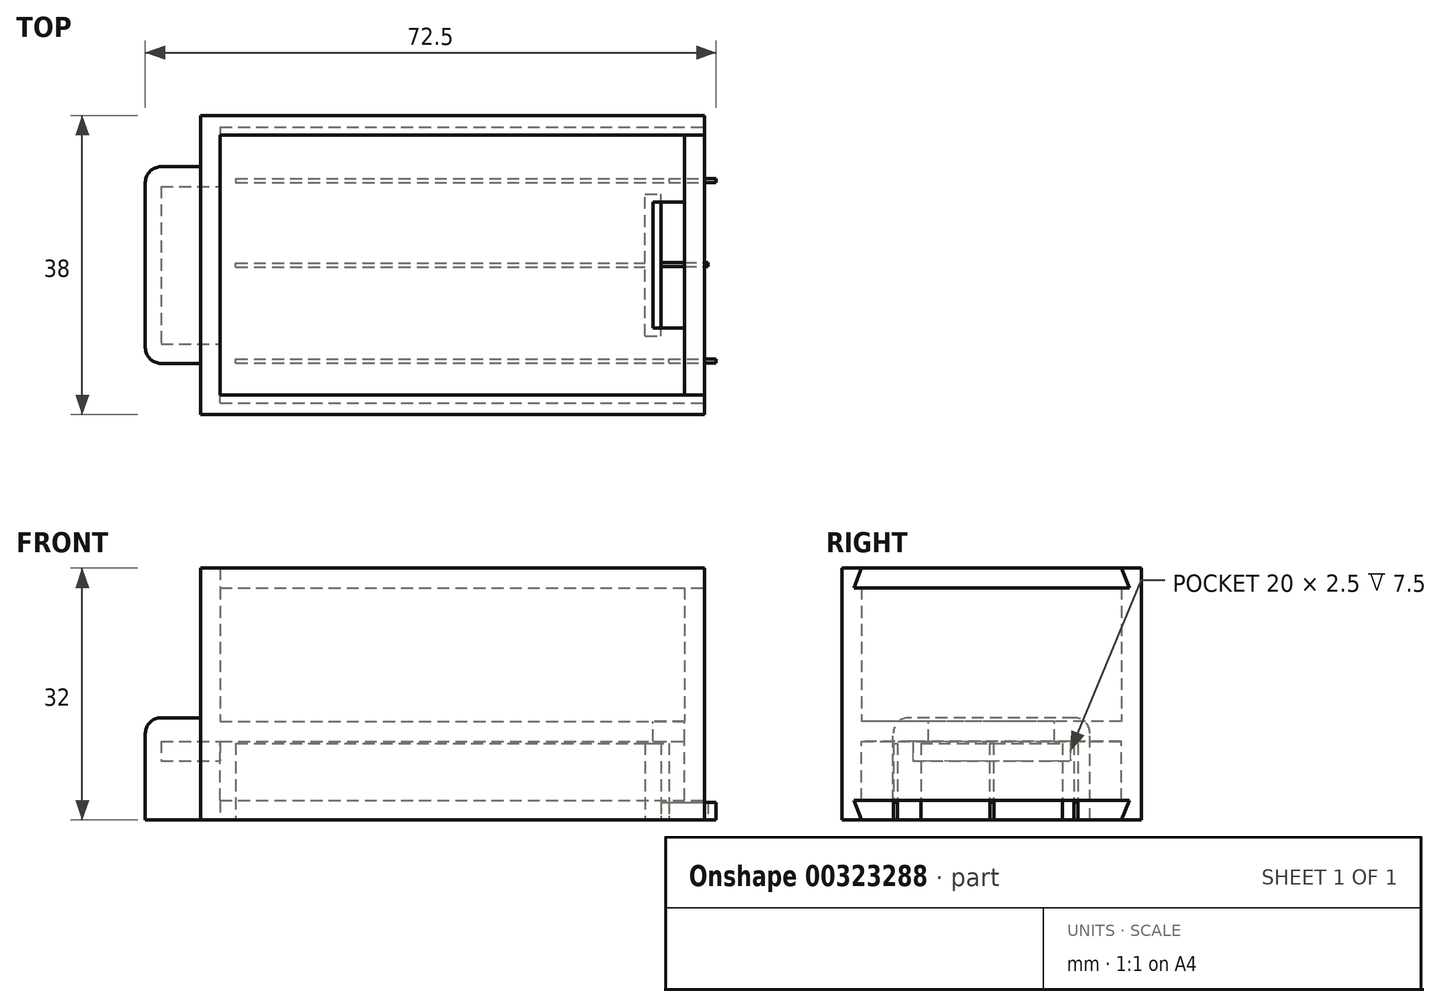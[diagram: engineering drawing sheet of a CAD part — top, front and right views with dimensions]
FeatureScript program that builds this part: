
annotation { "Feature Type Name" : "Feature", "Feature Type Description" : "" }
export const myFeature = defineFeature(function(context is Context, id is Id, definition is map)
    precondition{}
    {
        {
            var Q0;
            Q0=qCreatedBy(makeId("Top.planeOp"),FACE);
            var sketch = newSketch(context, id + "F0", { "sketchPlane" : qUnion([Q0])});
            skLineSegment(sketch, "E0.bottom", {"start": v(-32, 19) * mm, "end": v(32, 19) * mm});
            skLineSegment(sketch, "E0.top", {"start": v(-32, -19) * mm, "end": v(32, -19) * mm});
            skLineSegment(sketch, "E0.left", {"start": v(-32, 19) * mm, "end": v(-32, -19) * mm});
            skLineSegment(sketch, "E0.right", {"start": v(32, 19) * mm, "end": v(32, -19) * mm});
            skPoint(sketch, "E1", {"position": v(32, 0) * mm});
            skPoint(sketch, "E2", {"position": v(0, -19) * mm});
            skSolve(sketch);
        }
        {
            var Q0;
            Q0=makeQuery(id+"F0.imprint","IMPRINT",FACE,{"disambiguationData":[TD([[makeQuery(id+"F0.imprint","IMPRINT",EDGE,{"derivedFrom":sQuery(id+"F0.wireOp",EDGE,"E0.bottom")}),-1.0]])]});
            extrude(context, id + "F1", {"entities" : qUnion([Q0]), "depth" : 22 * mm});
        }
        {
            var Q0;
            Q0=makeQuery(id+"F1.opExtrude","CAP_FACE",FACE,{"disambiguationData":[OSD([sQuery(id+"F0.wireOp",EDGE,"E0.bottom"),sQuery(id+"F0.wireOp",EDGE,"E0.top"),sQuery(id+"F0.wireOp",EDGE,"E0.left"),sQuery(id+"F0.wireOp",EDGE,"E0.right")])],"isStart":false});
            shell(context, id + "F2", {"entities" : qUnion([Q0]), "thickness" : 2.5 * mm});
        }
        {
            var Q0;
            Q0=makeQuery(id+"F1.opExtrude","SWEPT_FACE",FACE,{"disambiguationData":[OSD([sQuery(id+"F0.wireOp",EDGE,"E0.right")])]});
            var sketch = newSketch(context, id + "F3", { "sketchPlane" : qUnion([Q0])});
            skLineSegment(sketch, "E3.bottom", {"start": v(19, 22) * mm, "end": v(-19, 22) * mm});
            skLineSegment(sketch, "E3.top", {"start": v(19, 19.5) * mm, "end": v(-19, 19.5) * mm});
            skLineSegment(sketch, "E3.left", {"start": v(19, 22) * mm, "end": v(19, 19.5) * mm});
            skLineSegment(sketch, "E3.right", {"start": v(-19, 22) * mm, "end": v(-19, 19.5) * mm});
            skPoint(sketch, "E4", {"position": v(17.5, 19.5) * mm});
            skPoint(sketch, "E5", {"position": v(-17.5, 19.5) * mm});
            skLineSegment(sketch, "E6", {"start": v(-16.5, 22) * mm, "end": v(-17.5, 19.5) * mm});
            skLineSegment(sketch, "E7", {"start": v(16.5, 22) * mm, "end": v(17.5, 19.5) * mm});
            skLineSegment(sketch, "E8", {"start": v(-17.2, 19.5) * mm, "end": v(-16.2, 22) * mm});
            skLineSegment(sketch, "E9", {"start": v(17.2, 19.5) * mm, "end": v(16.2, 22) * mm});
            skSolve(sketch);
        }
        {
            var Q0;
            {var subQ0=sQuery(id+"F3.wireOp",EDGE,"E7");Q0=makeQuery(id+"F3.imprint","IMPRINT",FACE,{"disambiguationData":[TD([[makeQuery(id+"F3.imprint","IMPRINT",EDGE,{"derivedFrom":subQ0}),-1.0]])]});}
            var Q1;
            {var subQ0=sQuery(id+"F3.wireOp",EDGE,"E8");Q1=makeQuery(id+"F3.imprint","IMPRINT",FACE,{"disambiguationData":[TD([[makeQuery(id+"F3.imprint","IMPRINT",EDGE,{"derivedFrom":subQ0}),-1.0]])]});}
            var Q2;
            {var subQ0=sQuery(id+"F3.wireOp",EDGE,"E6");Q2=makeQuery(id+"F3.imprint","IMPRINT",FACE,{"disambiguationData":[TD([[makeQuery(id+"F3.imprint","IMPRINT",EDGE,{"derivedFrom":subQ0}),1.0]])]});}
            var Q3;
            {var subQ0=sQuery(id+"F0.wireOp",EDGE,"E0.left");var subQ1=sQuery(id+"F0.wireOp",EDGE,"E0.bottom");Q3=makeQuery(id+"F2.opShell","OFFSET_VERTEX",VERTEX,{"disambiguationData":[OSD([subQ1,subQ0]),TDD([makeQuery(id+"F1.opExtrude","CAP_VERTEX",VERTEX,{"disambiguationData":[OSD([subQ1,subQ0])],"isStart":false})])]});}
            extrude(context, id + "F4", {"entities" : qUnion([Q0, Q1, Q2]), "operationType" : NewBodyOperationType.REMOVE, "endBound" : BoundingType.UP_TO_VERTEX, "oppositeDirection" : true, "endBoundEntityVertex" : qUnion([Q3]), "depth" : 25 * mm});
        }
        {
            var Q0;
            {var subQ0=sQuery(id+"F3.wireOp",EDGE,"E8");Q0=makeQuery(id+"F3.imprint","IMPRINT",FACE,{"disambiguationData":[TD([[makeQuery(id+"F3.imprint","IMPRINT",EDGE,{"derivedFrom":subQ0}),-1.0]])]});}
            var Q1;
            {var subQ0=sQuery(id+"F0.wireOp",EDGE,"E0.left");var subQ1=sQuery(id+"F0.wireOp",EDGE,"E0.bottom");Q1=makeQuery(id+"F4.boolean.opBoolean","MERGE",VERTEX,{"derivedFrom":[makeQuery(id+"F2.opShell","OFFSET_VERTEX",VERTEX,{"disambiguationData":[OSD([subQ1,subQ0]),TDD([makeQuery(id+"F1.opExtrude","CAP_VERTEX",VERTEX,{"disambiguationData":[OSD([subQ1,subQ0])],"isStart":false})])]})],"fromTools":[makeQuery(id+"F4.opExtrude","CAP_VERTEX",VERTEX,{"disambiguationData":[OSD([sQuery(id+"F3.wireOp",EDGE,"E3.bottom"),sQuery(id+"F3.wireOp",EDGE,"E7")])],"isStart":false})]});}
            extrude(context, id + "F5", {"entities" : qUnion([Q0]), "endBound" : BoundingType.UP_TO_VERTEX, "oppositeDirection" : true, "endBoundEntityVertex" : qUnion([Q1]), "depth" : 25 * mm});
        }
        {
            var Q0;
            Q0=makeQuery(id+"F2.opShell","OFFSET_FACE",FACE,{"disambiguationData":[OSD([sQuery(id+"F0.wireOp",EDGE,"E0.bottom"),sQuery(id+"F0.wireOp",EDGE,"E0.top"),sQuery(id+"F0.wireOp",EDGE,"E0.left"),sQuery(id+"F0.wireOp",EDGE,"E0.right")])]});
            var sketch = newSketch(context, id + "F6", { "sketchPlane" : qUnion([Q0])});
            skLineSegment(sketch, "E10.bottom", {"start": v(29.5, 8) * mm, "end": v(25.5, 8) * mm});
            skLineSegment(sketch, "E10.top", {"start": v(29.5, -8) * mm, "end": v(25.5, -8) * mm});
            skLineSegment(sketch, "E10.left", {"start": v(29.5, 8) * mm, "end": v(29.5, -8) * mm});
            skLineSegment(sketch, "E10.right", {"start": v(25.5, 8) * mm, "end": v(25.5, -8) * mm});
            skPoint(sketch, "E11", {"position": v(29.5, 0) * mm});
            skSolve(sketch);
        }
        {
            var Q0;
            Q0=makeQuery(id+"F6.imprint","IMPRINT",FACE,{"disambiguationData":[TD([[makeQuery(id+"F6.imprint","IMPRINT",EDGE,{"derivedFrom":sQuery(id+"F6.wireOp",EDGE,"E10.bottom")}),1.0]])]});
            var Q1;
            Q1=makeQuery(id+"F1.opExtrude","CAP_FACE",FACE,{"disambiguationData":[OSD([sQuery(id+"F0.wireOp",EDGE,"E0.bottom"),sQuery(id+"F0.wireOp",EDGE,"E0.top"),sQuery(id+"F0.wireOp",EDGE,"E0.left"),sQuery(id+"F0.wireOp",EDGE,"E0.right")])],"isStart":true});
            extrude(context, id + "F7", {"entities" : qUnion([Q0]), "operationType" : NewBodyOperationType.REMOVE, "endBound" : BoundingType.UP_TO_SURFACE, "oppositeDirection" : true, "endBoundEntityFace" : qUnion([Q1]), "depth" : 25 * mm});
        }
        {
            var Q0;
            Q0=makeQuery(id+"F1.opExtrude","CAP_FACE",FACE,{"disambiguationData":[OSD([sQuery(id+"F0.wireOp",EDGE,"E0.bottom"),sQuery(id+"F0.wireOp",EDGE,"E0.top"),sQuery(id+"F0.wireOp",EDGE,"E0.left"),sQuery(id+"F0.wireOp",EDGE,"E0.right")])],"isStart":true});
            var sketch = newSketch(context, id + "F8", { "sketchPlane" : qUnion([Q0])});
            skLineSegment(sketch, "E12.0", {"start": v(-29.5, 16.5) * mm, "end": v(29.5, 16.5) * mm});
            skLineSegment(sketch, "E12.1", {"start": v(-29.5, -16.5) * mm, "end": v(-29.5, 16.5) * mm});
            skLineSegment(sketch, "E12.2", {"start": v(-29.5, -16.5) * mm, "end": v(29.5, -16.5) * mm});
            skLineSegment(sketch, "E12.3", {"start": v(29.5, -16.5) * mm, "end": v(29.5, 16.5) * mm});
            skSolve(sketch);
        }
        {
            var Q0;
            {var subQ8=sQuery(id+"F8.wireOp",EDGE,"E12.0");Q0=makeQuery(id+"F8.imprint","IMPRINT",FACE,{"disambiguationData":[TD([[makeQuery(id+"F8.imprint","IMPRINT",EDGE,{"derivedFrom":subQ8}),1.0]])]});}
            extrude(context, id + "F9", {"entities" : qUnion([Q0]), "operationType" : NewBodyOperationType.ADD, "depth" : 10 * mm});
        }
        {
            var Q0;
            Q0=makeQuery(id+"F9.opExtrude","SWEPT_FACE",FACE,{"disambiguationData":[OSD([sQuery(id+"F8.wireOp",EDGE,"E12.1")])]});
            var sketch = newSketch(context, id + "F10", { "sketchPlane" : qUnion([Q0])});
            skLineSegment(sketch, "E13.bottom", {"start": v(-10, 0) * mm, "end": v(10, 0) * mm});
            skLineSegment(sketch, "E13.top", {"start": v(-10, -2.5) * mm, "end": v(10, -2.5) * mm});
            skLineSegment(sketch, "E13.left", {"start": v(-10, 0) * mm, "end": v(-10, -2.5) * mm});
            skLineSegment(sketch, "E13.right", {"start": v(10, 0) * mm, "end": v(10, -2.5) * mm});
            skPoint(sketch, "E14", {"position": v(0, 0) * mm});
            skSolve(sketch);
        }
        {
            var Q0;
            Q0=makeQuery(id+"F10.imprint","IMPRINT",FACE,{"disambiguationData":[TD([[makeQuery(id+"F10.imprint","IMPRINT",EDGE,{"derivedFrom":sQuery(id+"F10.wireOp",EDGE,"E13.bottom")}),1.0]])]});
            extrude(context, id + "F11", {"entities" : qUnion([Q0]), "operationType" : NewBodyOperationType.REMOVE, "endBound" : BoundingType.THROUGH_ALL, "oppositeDirection" : true, "depth" : 25 * mm});
        }
        {
            var Q0;
            {var subQ0=sQuery(id+"F0.wireOp",EDGE,"E0.right");Q0=makeQuery(id+"F9.boolean.opBoolean","MERGE",FACE,{"derivedFrom":[makeQuery(id+"F1.opExtrude","SWEPT_FACE",FACE,{"disambiguationData":[OSD([subQ0])]}),makeQuery(id+"F9.opExtrude","SWEPT_FACE",FACE,{"disambiguationData":[OSD([subQ0])]})]});}
            var sketch = newSketch(context, id + "F12", { "sketchPlane" : qUnion([Q0])});
            skLineSegment(sketch, "E15", {"start": v(-19, -7.5) * mm, "end": v(19, -7.5) * mm});
            skLineSegment(sketch, "E16", {"start": v(-17.5, -7.5) * mm, "end": v(-16.5, -10) * mm});
            skLineSegment(sketch, "E17", {"start": v(17.5, -7.5) * mm, "end": v(16.5, -10) * mm});
            skLineSegment(sketch, "E18", {"start": v(-17.2, -7.5) * mm, "end": v(-16.2, -10) * mm});
            skLineSegment(sketch, "E19", {"start": v(17.2, -7.5) * mm, "end": v(16.2, -10) * mm});
            skSolve(sketch);
        }
        {
            var Q0;
            {var subQ0=sQuery(id+"F12.wireOp",EDGE,"E18");Q0=makeQuery(id+"F12.imprint","IMPRINT",FACE,{"disambiguationData":[TD([[makeQuery(id+"F12.imprint","IMPRINT",EDGE,{"derivedFrom":subQ0}),1.0]])]});}
            var Q1;
            {var subQ0=sQuery(id+"F12.wireOp",EDGE,"E17");Q1=makeQuery(id+"F12.imprint","IMPRINT",FACE,{"disambiguationData":[TD([[makeQuery(id+"F12.imprint","IMPRINT",EDGE,{"derivedFrom":subQ0}),-1.0]])]});}
            var Q2;
            {var subQ0=sQuery(id+"F12.wireOp",EDGE,"E16");Q2=makeQuery(id+"F12.imprint","IMPRINT",FACE,{"disambiguationData":[TD([[makeQuery(id+"F12.imprint","IMPRINT",EDGE,{"derivedFrom":subQ0}),1.0]])]});}
            var Q3;
            Q3=makeQuery(id+"F9.opExtrude","SWEPT_FACE",FACE,{"disambiguationData":[OSD([sQuery(id+"F8.wireOp",EDGE,"E12.1")])]});
            extrude(context, id + "F13", {"entities" : qUnion([Q0, Q1, Q2]), "operationType" : NewBodyOperationType.REMOVE, "endBound" : BoundingType.UP_TO_SURFACE, "oppositeDirection" : true, "endBoundEntityFace" : qUnion([Q3]), "depth" : 25 * mm});
        }
        {
            var Q0;
            {var subQ0=sQuery(id+"F12.wireOp",EDGE,"E18");Q0=makeQuery(id+"F12.imprint","IMPRINT",FACE,{"disambiguationData":[TD([[makeQuery(id+"F12.imprint","IMPRINT",EDGE,{"derivedFrom":subQ0}),1.0]])]});}
            var Q1;
            Q1=makeQuery(id+"F13.boolean.opBoolean","MERGE",FACE,{"derivedFrom":[makeQuery(id+"F9.opExtrude","SWEPT_FACE",FACE,{"disambiguationData":[OSD([sQuery(id+"F8.wireOp",EDGE,"E12.1")])]})],"fromTools":[makeQuery(id+"F13.opExtrude","CAP_FACE",FACE,{"disambiguationData":[OSD([sQuery(id+"F0.wireOp",EDGE,"E0.right"),sQuery(id+"F12.wireOp",EDGE,"E15"),sQuery(id+"F12.wireOp",EDGE,"E16"),sQuery(id+"F12.wireOp",EDGE,"E17")])],"isStart":false})]});
            extrude(context, id + "F14", {"entities" : qUnion([Q0]), "endBound" : BoundingType.UP_TO_SURFACE, "oppositeDirection" : true, "endBoundEntityFace" : qUnion([Q1]), "depth" : 25 * mm});
        }
        {
            var Q0;
            Q0=makeQuery(id+"F9.opExtrude","CAP_FACE",FACE,{"disambiguationData":[OSD([sQuery(id+"F0.wireOp",EDGE,"E0.bottom"),sQuery(id+"F0.wireOp",EDGE,"E0.top"),sQuery(id+"F0.wireOp",EDGE,"E0.left"),sQuery(id+"F0.wireOp",EDGE,"E0.right"),sQuery(id+"F8.wireOp",EDGE,"E12.0"),sQuery(id+"F8.wireOp",EDGE,"E12.1"),sQuery(id+"F8.wireOp",EDGE,"E12.2"),sQuery(id+"F8.wireOp",EDGE,"E12.3")])],"isStart":false});
            var sketch = newSketch(context, id + "F15", { "sketchPlane" : qUnion([Q0])});
            skPoint(sketch, "E20.0", {"position": v(25.5, -8) * mm});
            skPoint(sketch, "E20.1", {"position": v(25.5, 8) * mm});
            skLineSegment(sketch, "E21.bottom", {"start": v(24.5, 9) * mm, "end": v(26.5, 9) * mm});
            skLineSegment(sketch, "E21.top", {"start": v(24.5, -9) * mm, "end": v(26.5, -9) * mm});
            skLineSegment(sketch, "E21.left", {"start": v(24.5, 9) * mm, "end": v(24.5, -9) * mm});
            skLineSegment(sketch, "E21.right", {"start": v(26.5, 9) * mm, "end": v(26.5, -9) * mm});
            skLineSegment(sketch, "E22.bottom", {"start": v(-27.5, 0.25) * mm, "end": v(24.5, 0.25) * mm});
            skLineSegment(sketch, "E22.top", {"start": v(-27.5, -0.25) * mm, "end": v(24.5, -0.25) * mm});
            skLineSegment(sketch, "E22.left", {"start": v(-27.5, 0.25) * mm, "end": v(-27.5, -0.25) * mm});
            skLineSegment(sketch, "E22.right", {"start": v(24.5, 0.25) * mm, "end": v(24.5, -0.25) * mm});
            skLineSegment(sketch, "E23.bottom", {"start": v(-27.5, -10.99) * mm, "end": v(27.5, -10.99) * mm});
            skLineSegment(sketch, "E23.top", {"start": v(-27.5, -10.49) * mm, "end": v(27.5, -10.49) * mm});
            skLineSegment(sketch, "E23.left", {"start": v(-27.5, -10.99) * mm, "end": v(-27.5, -10.49) * mm});
            skLineSegment(sketch, "E23.right", {"start": v(27.5, -10.99) * mm, "end": v(27.5, -10.49) * mm});
            skLineSegment(sketch, "E24.bottom", {"start": v(-27.5, 12.45) * mm, "end": v(27.5, 12.45) * mm});
            skLineSegment(sketch, "E24.top", {"start": v(-27.5, 11.95) * mm, "end": v(27.5, 11.95) * mm});
            skLineSegment(sketch, "E24.left", {"start": v(-27.5, 12.45) * mm, "end": v(-27.5, 11.95) * mm});
            skLineSegment(sketch, "E24.right", {"start": v(27.5, 12.45) * mm, "end": v(27.5, 11.95) * mm});
            skLineSegment(sketch, "E25.bottom", {"start": v(27.5, 12.45) * mm, "end": v(33.5, 12.45) * mm});
            skLineSegment(sketch, "E25.top", {"start": v(27.5, 11.95) * mm, "end": v(33.5, 11.95) * mm});
            skLineSegment(sketch, "E25.right", {"start": v(33.5, 12.45) * mm, "end": v(33.5, 11.95) * mm});
            skLineSegment(sketch, "E26.bottom", {"start": v(27.5, -10.49) * mm, "end": v(33.5, -10.49) * mm});
            skLineSegment(sketch, "E26.top", {"start": v(27.5, -10.99) * mm, "end": v(33.5, -10.99) * mm});
            skLineSegment(sketch, "E26.left", {"start": v(27.5, -10.49) * mm, "end": v(27.5, -10.99) * mm});
            skLineSegment(sketch, "E26.right", {"start": v(33.5, -10.49) * mm, "end": v(33.5, -10.99) * mm});
            skLineSegment(sketch, "E27.bottom", {"start": v(26.5, 0.21) * mm, "end": v(32.5, 0.21) * mm});
            skLineSegment(sketch, "E27.top", {"start": v(26.5, -0.29) * mm, "end": v(32.5, -0.29) * mm});
            skLineSegment(sketch, "E27.left", {"start": v(26.5, 0.21) * mm, "end": v(26.5, -0.29) * mm});
            skLineSegment(sketch, "E27.right", {"start": v(32.5, 0.21) * mm, "end": v(32.5, -0.29) * mm});
            skPoint(sketch, "E28", {"position": v(24.5, 0) * mm});
            skPoint(sketch, "E29", {"position": v(26.5, 0) * mm});
            skSolve(sketch);
        }
        {
            var Q0;
            Q0=makeQuery(id+"F15.imprint","IMPRINT",FACE,{"disambiguationData":[TD([[makeQuery(id+"F15.imprint","IMPRINT",EDGE,{"derivedFrom":sQuery(id+"F15.wireOp",EDGE,"E22.bottom")}),-1.0]])]});
            var Q1;
            {var subQ3=sQuery(id+"F15.wireOp",EDGE,"E21.bottom");Q1=makeQuery(id+"F15.imprint","IMPRINT",FACE,{"disambiguationData":[TD([[makeQuery(id+"F15.imprint","IMPRINT",EDGE,{"derivedFrom":subQ3}),-1.0]])]});}
            var Q2;
            {var subQ0=sQuery(id+"F15.wireOp",EDGE,"E23.bottom");Q2=makeQuery(id+"F15.imprint","IMPRINT",FACE,{"disambiguationData":[TD([[makeQuery(id+"F15.imprint","IMPRINT",EDGE,{"derivedFrom":subQ0}),1.0]])]});}
            var Q3;
            Q3=makeQuery(id+"F15.imprint","IMPRINT",FACE,{"disambiguationData":[TD([[makeQuery(id+"F15.imprint","IMPRINT",EDGE,{"derivedFrom":sQuery(id+"F15.wireOp",EDGE,"E24.bottom")}),-1.0]])]});
            extrude(context, id + "F16", {"entities" : qUnion([Q0, Q1, Q2, Q3]), "oppositeDirection" : true, "depth" : 9.75 * mm});
        }
        {
            var Q0;
            Q0=makeQuery(id+"F15.imprint","IMPRINT",FACE,{"disambiguationData":[TD([[makeQuery(id+"F15.imprint","IMPRINT",EDGE,{"derivedFrom":sQuery(id+"F15.wireOp",EDGE,"E25.bottom")}),-1.0]])]});
            var Q1;
            {var subQ3=sQuery(id+"F15.wireOp",EDGE,"E26.bottom");Q1=makeQuery(id+"F15.imprint","IMPRINT",FACE,{"disambiguationData":[TD([[makeQuery(id+"F15.imprint","IMPRINT",EDGE,{"derivedFrom":subQ3}),-1.0]])]});}
            var Q2;
            Q2=makeQuery(id+"F15.imprint","IMPRINT",FACE,{"disambiguationData":[TD([[makeQuery(id+"F15.imprint","IMPRINT",EDGE,{"derivedFrom":sQuery(id+"F15.wireOp",EDGE,"E27.bottom")}),-1.0]])]});
            extrude(context, id + "F17", {"entities" : qUnion([Q0, Q1, Q2]), "oppositeDirection" : true, "depth" : 2.25 * mm});
        }
        {
            var Q0;
            Q0=makeQuery(id+"F14.opExtrude","SWEPT_BODY",BODY,{"disambiguationData":[OSD([sQuery(id+"F0.wireOp",EDGE,"E0.right"),sQuery(id+"F12.wireOp",EDGE,"E15"),sQuery(id+"F12.wireOp",EDGE,"E18"),sQuery(id+"F12.wireOp",EDGE,"E19")])]});
            deleteBodies(context, id + "F18", {"entities" : qUnion([Q0])});
        }
        {
            var Q0;
            Q0=makeQuery(id+"F5.opExtrude","SWEPT_BODY",BODY,{"disambiguationData":[OSD([sQuery(id+"F3.wireOp",EDGE,"E3.bottom"),sQuery(id+"F3.wireOp",EDGE,"E3.top"),sQuery(id+"F3.wireOp",EDGE,"E8"),sQuery(id+"F3.wireOp",EDGE,"E9")])]});
            deleteBodies(context, id + "F19", {"entities" : qUnion([Q0])});
        }
        {
            var Q0;
            {var subQ0=sQuery(id+"F0.wireOp",EDGE,"E0.left");Q0=makeQuery(id+"F9.boolean.opBoolean","MERGE",FACE,{"derivedFrom":[makeQuery(id+"F1.opExtrude","SWEPT_FACE",FACE,{"disambiguationData":[OSD([subQ0])]}),makeQuery(id+"F9.opExtrude","SWEPT_FACE",FACE,{"disambiguationData":[OSD([subQ0])]})]});}
            var sketch = newSketch(context, id + "F20", { "sketchPlane" : qUnion([Q0])});
            skLineSegment(sketch, "E30.bottom", {"start": v(-12.5, -10) * mm, "end": v(12.5, -10) * mm});
            skLineSegment(sketch, "E30.top", {"start": v(-12.5, 3) * mm, "end": v(12.5, 3) * mm});
            skLineSegment(sketch, "E30.left", {"start": v(-12.5, -10) * mm, "end": v(-12.5, 3) * mm});
            skLineSegment(sketch, "E30.right", {"start": v(12.5, -10) * mm, "end": v(12.5, 3) * mm});
            skPoint(sketch, "E31", {"position": v(0, 3) * mm});
            skSolve(sketch);
        }
        {
            var Q0;
            Q0=makeQuery(id+"F20.imprint","IMPRINT",FACE,{"disambiguationData":[TD([[makeQuery(id+"F20.imprint","IMPRINT",EDGE,{"derivedFrom":sQuery(id+"F20.wireOp",EDGE,"E30.bottom")}),1.0]])]});
            var Q1;
            {var subQ0=sQuery(id+"F0.wireOp",EDGE,"E0.left");var subQ1=makeQuery(id+"F9.boolean.opBoolean","MERGE",FACE,{"derivedFrom":[makeQuery(id+"F1.opExtrude","SWEPT_FACE",FACE,{"disambiguationData":[OSD([subQ0])]}),makeQuery(id+"F9.opExtrude","SWEPT_FACE",FACE,{"disambiguationData":[OSD([subQ0])]})]});Q1=makeQuery(id+"F20.imprint","IMPRINT",FACE,{"disambiguationData":[TD([[makeQuery(id+"F20.imprint","IMPRINT",EDGE,{"derivedFrom":makeQuery(id+"F11.boolean.opBoolean","INTERSECT",EDGE,{"derivedFrom":[subQ1,makeQuery(id+"F11.opExtrude","SWEPT_FACE",FACE,{"disambiguationData":[OSD([sQuery(id+"F10.wireOp",EDGE,"E13.bottom")])]})]})}),-1.0]])]});}
            extrude(context, id + "F21", {"entities" : qUnion([Q0, Q1]), "operationType" : NewBodyOperationType.ADD, "depth" : 7 * mm});
        }
        {
            var Q0;
            Q0=makeQuery(id+"F21.opExtrude","CAP_FACE",FACE,{"disambiguationData":[OSD([sQuery(id+"F20.wireOp",EDGE,"E30.bottom"),sQuery(id+"F20.wireOp",EDGE,"E30.top"),sQuery(id+"F20.wireOp",EDGE,"E30.left"),sQuery(id+"F20.wireOp",EDGE,"E30.right")])],"isStart":true});
            extrude(context, id + "F22", {"entities" : qUnion([Q0]), "operationType" : NewBodyOperationType.REMOVE, "oppositeDirection" : true, "depth" : 5 * mm});
        }
        {
            var Q0;
            Q0=makeQuery(id+"F21.opExtrude","CAP_EDGE",EDGE,{"disambiguationData":[OSD([sQuery(id+"F20.wireOp",EDGE,"E30.top")])],"isStart":false});
            var Q1;
            Q1=makeQuery(id+"F21.opExtrude","SWEPT_EDGE",EDGE,{"disambiguationData":[OSD([sQuery(id+"F20.wireOp",EDGE,"E30.top"),sQuery(id+"F20.wireOp",EDGE,"E30.left")])]});
            var Q2;
            Q2=makeQuery(id+"F21.opExtrude","SWEPT_EDGE",EDGE,{"disambiguationData":[OSD([sQuery(id+"F20.wireOp",EDGE,"E30.top"),sQuery(id+"F20.wireOp",EDGE,"E30.right")])]});
            var Q3;
            Q3=makeQuery(id+"F21.opExtrude","CAP_EDGE",EDGE,{"disambiguationData":[OSD([sQuery(id+"F20.wireOp",EDGE,"E30.right")])],"isStart":false});
            var Q4;
            Q4=makeQuery(id+"F21.opExtrude","CAP_EDGE",EDGE,{"disambiguationData":[OSD([sQuery(id+"F20.wireOp",EDGE,"E30.left")])],"isStart":false});
            var Q5;
            Q5=makeQuery(id+"F21.opExtrude","CAP_EDGE",EDGE,{"disambiguationData":[OSD([sQuery(id+"F20.wireOp",EDGE,"E30.left")])],"isStart":true});
            fillet(context, id + "F23", {"entities" : qUnion([Q0, Q1, Q2, Q3, Q4, Q5]), "radius" : 2 * mm, "tangentPropagation" : true, "allowEdgeOverflow" : false});
        }
    });
